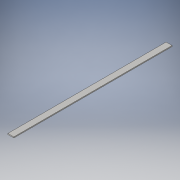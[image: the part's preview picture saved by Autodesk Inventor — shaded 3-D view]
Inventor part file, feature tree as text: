
AUTODESK INVENTOR PART (.ipt)
format: ipt  version: 2016 (Build 200138000, 138)  size: 103,936 bytes
history: native  units: in
note: dims shown in document units (in); Inventor stores cm internally (conversion verified against a paired STEP export)
features: extrude x1, sketch x1
ambient origin geometry x8: Origin, YZ Plane, XZ Plane, XY Plane, X Axis, Y Axis, Z Axis, Center Point
bodies: Solid1 (feature_tree)
feature tree (2):
  extrude  "Extrusion1"  Depth=31.4961in
  sketch  "Sketch1"  dims[d0=1.1811in d1=31.4961in d2=0.1969in d3=0.0in]
